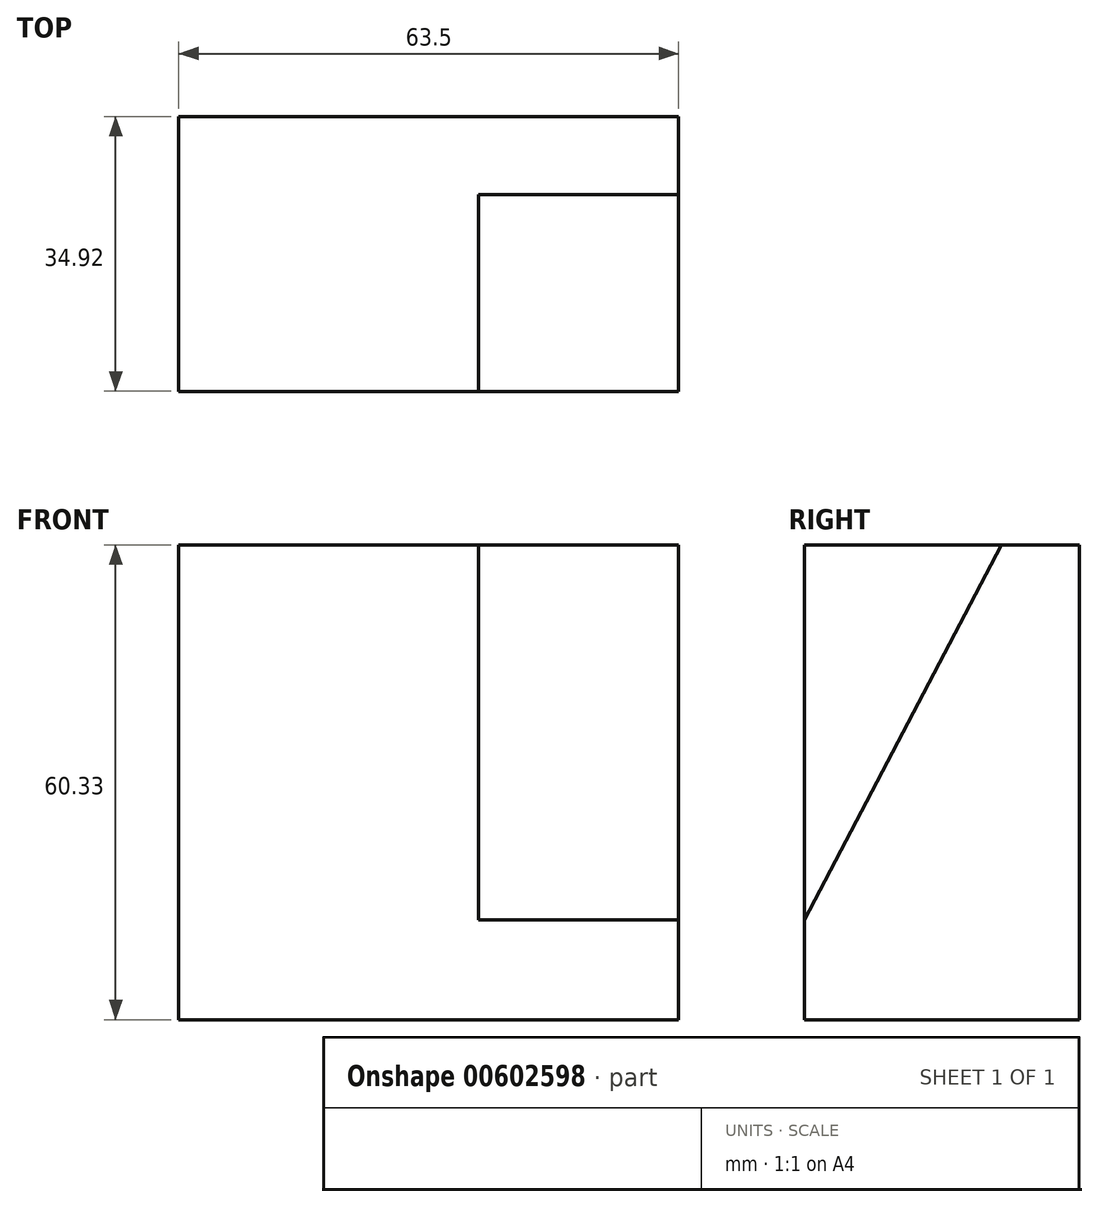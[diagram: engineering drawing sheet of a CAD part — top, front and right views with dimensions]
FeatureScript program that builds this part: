
annotation { "Feature Type Name" : "Feature", "Feature Type Description" : "" }
export const myFeature = defineFeature(function(context is Context, id is Id, definition is map)
    precondition{}
    {
        {
            var Q0;
            Q0=qCreatedBy(makeId("Front.planeOp"),FACE);
            var sketch = newSketch(context, id + "F0", { "sketchPlane" : qUnion([Q0])});
            skLineSegment(sketch, "E0.bottom", {"start": v(0, 0) * mm, "end": v(38.1, 0) * mm});
            skLineSegment(sketch, "E0.top", {"start": v(0, 60.33) * mm, "end": v(38.1, 60.33) * mm});
            skLineSegment(sketch, "E0.left", {"start": v(0, 0) * mm, "end": v(0, 60.33) * mm});
            skLineSegment(sketch, "E0.right", {"start": v(38.1, 0) * mm, "end": v(38.1, 60.33) * mm});
            skSolve(sketch);
        }
        {
            var Q0;
            Q0=makeQuery(id+"F0.imprint","IMPRINT",FACE,{"disambiguationData":[TD([[makeQuery(id+"F0.imprint","IMPRINT",EDGE,{"derivedFrom":sQuery(id+"F0.wireOp",EDGE,"E0.bottom")}),1.0]])]});
            extrude(context, id + "F1", {"entities" : qUnion([Q0]), "depth" : 34.92 * mm, "offsetDistance" : 25.4 * mm});
        }
        {
            var Q0;
            Q0=makeQuery(id+"F1.opExtrude","SWEPT_FACE",FACE,{"disambiguationData":[OSD([sQuery(id+"F0.wireOp",EDGE,"E0.right")])]});
            var sketch = newSketch(context, id + "F2", { "sketchPlane" : qUnion([Q0])});
            skLineSegment(sketch, "E1", {"start": v(-34.92, 12.7) * mm, "end": v(-9.92, 60.32) * mm});
            skLineSegment(sketch, "E2", {"start": v(-9.92, 60.33) * mm, "end": v(-9.92, 12.7) * mm});
            skLineSegment(sketch, "E3", {"start": v(-9.92, 12.7) * mm, "end": v(-34.93, 12.7) * mm});
            skSolve(sketch);
        }
        {
            var Q0;
            Q0=makeQuery(id+"F2.imprint","IMPRINT",FACE,{"disambiguationData":[TD([[makeQuery(id+"F2.imprint","IMPRINT",EDGE,{"derivedFrom":sQuery(id+"F2.wireOp",EDGE,"E1")}),-1.0]])]});
            extrude(context, id + "F3", {"entities" : qUnion([Q0]), "operationType" : NewBodyOperationType.ADD, "depth" : 25.4 * mm, "offsetDistance" : 25.4 * mm});
        }
        {
            var Q0;
            {var subQ0=sQuery(id+"F0.wireOp",EDGE,"E0.top");var subQ1=sQuery(id+"F0.wireOp",EDGE,"E0.right");var subQ2=sQuery(id+"F0.wireOp",EDGE,"E0.left");var subQ3=sQuery(id+"F0.wireOp",EDGE,"E0.bottom");var subQ4=makeQuery(id+"F1.opExtrude","SWEPT_FACE",FACE,{"disambiguationData":[OSD([subQ1])]});Q0=makeQuery(id+"F3.boolean.opBoolean","SPLIT",FACE,{"disambiguationData":[TD([makeQuery(id+"F1.opExtrude","SWEPT_FACE",FACE,{"disambiguationData":[OSD([subQ3])]}),makeQuery(id+"F1.opExtrude","CAP_FACE",FACE,{"disambiguationData":[OSD([subQ3,subQ0,subQ2,subQ1])],"isStart":true}),makeQuery(id+"F1.opExtrude","CAP_FACE",FACE,{"disambiguationData":[OSD([subQ3,subQ0,subQ2,subQ1])],"isStart":false}),makeQuery(id+"F1.opExtrude","SWEPT_FACE",FACE,{"disambiguationData":[OSD([subQ0])]}),subQ4,makeQuery(id+"F3.opExtrude","SWEPT_FACE",FACE,{"disambiguationData":[OSD([sQuery(id+"F2.wireOp",EDGE,"E1")])]}),makeQuery(id+"F3.opExtrude","SWEPT_FACE",FACE,{"disambiguationData":[OSD([sQuery(id+"F2.wireOp",EDGE,"E2")])]}),makeQuery(id+"F3.opExtrude","SWEPT_FACE",FACE,{"disambiguationData":[OSD([sQuery(id+"F2.wireOp",EDGE,"E3")])]})])],"derivedFrom":subQ4});}
            var sketch = newSketch(context, id + "F4", { "sketchPlane" : qUnion([Q0])});
            skLineSegment(sketch, "E4", {"start": v(-9.92, 60.33) * mm, "end": v(-9.92, 0) * mm});
            skLineSegment(sketch, "E5", {"start": v(-9.92, 0) * mm, "end": v(0, 0) * mm});
            skLineSegment(sketch, "E6", {"start": v(0, 0) * mm, "end": v(0, 60.33) * mm});
            skLineSegment(sketch, "E7", {"start": v(0, 60.33) * mm, "end": v(-9.92, 60.33) * mm});
            skSolve(sketch);
        }
        {
            var Q0;
            {var subQ0=sQuery(id+"F4.wireOp",EDGE,"E5");Q0=makeQuery(id+"F4.imprint","IMPRINT",FACE,{"disambiguationData":[TD([[makeQuery(id+"F4.imprint","IMPRINT",EDGE,{"derivedFrom":subQ0}),1.0]])]});}
            extrude(context, id + "F5", {"entities" : qUnion([Q0]), "operationType" : NewBodyOperationType.ADD, "depth" : 25.4 * mm, "offsetDistance" : 25.4 * mm});
        }
        {
            var Q0;
            {var subQ0=sQuery(id+"F0.wireOp",EDGE,"E0.top");var subQ1=sQuery(id+"F0.wireOp",EDGE,"E0.right");var subQ2=sQuery(id+"F0.wireOp",EDGE,"E0.left");var subQ3=sQuery(id+"F0.wireOp",EDGE,"E0.bottom");var subQ4=makeQuery(id+"F1.opExtrude","SWEPT_FACE",FACE,{"disambiguationData":[OSD([subQ1])]});Q0=makeQuery(id+"F3.boolean.opBoolean","SPLIT",FACE,{"disambiguationData":[TD([makeQuery(id+"F1.opExtrude","SWEPT_FACE",FACE,{"disambiguationData":[OSD([subQ3])]}),makeQuery(id+"F1.opExtrude","CAP_FACE",FACE,{"disambiguationData":[OSD([subQ3,subQ0,subQ2,subQ1])],"isStart":true}),makeQuery(id+"F1.opExtrude","CAP_FACE",FACE,{"disambiguationData":[OSD([subQ3,subQ0,subQ2,subQ1])],"isStart":false}),makeQuery(id+"F1.opExtrude","SWEPT_FACE",FACE,{"disambiguationData":[OSD([subQ0])]}),subQ4,makeQuery(id+"F3.opExtrude","SWEPT_FACE",FACE,{"disambiguationData":[OSD([sQuery(id+"F2.wireOp",EDGE,"E1")])]}),makeQuery(id+"F3.opExtrude","SWEPT_FACE",FACE,{"disambiguationData":[OSD([sQuery(id+"F2.wireOp",EDGE,"E2")])]}),makeQuery(id+"F3.opExtrude","SWEPT_FACE",FACE,{"disambiguationData":[OSD([sQuery(id+"F2.wireOp",EDGE,"E3")])]})])],"derivedFrom":subQ4});}
            var sketch = newSketch(context, id + "F6", { "sketchPlane" : qUnion([Q0])});
            skLineSegment(sketch, "E8.bottom", {"start": v(-34.93, 0) * mm, "end": v(-9.92, 0) * mm});
            skLineSegment(sketch, "E8.top", {"start": v(-34.93, 12.7) * mm, "end": v(-9.92, 12.7) * mm});
            skLineSegment(sketch, "E8.left", {"start": v(-34.93, 0) * mm, "end": v(-34.93, 12.7) * mm});
            skLineSegment(sketch, "E8.right", {"start": v(-9.92, 0) * mm, "end": v(-9.92, 12.7) * mm});
            skSolve(sketch);
        }
        {
            var Q0;
            Q0=makeQuery(id+"F6.imprint","IMPRINT",FACE,{"disambiguationData":[TD([[makeQuery(id+"F6.imprint","IMPRINT",EDGE,{"derivedFrom":sQuery(id+"F6.wireOp",EDGE,"E8.bottom")}),1.0]])]});
            extrude(context, id + "F7", {"entities" : qUnion([Q0]), "operationType" : NewBodyOperationType.ADD, "depth" : 25.4 * mm, "offsetDistance" : 25.4 * mm});
        }
    });
